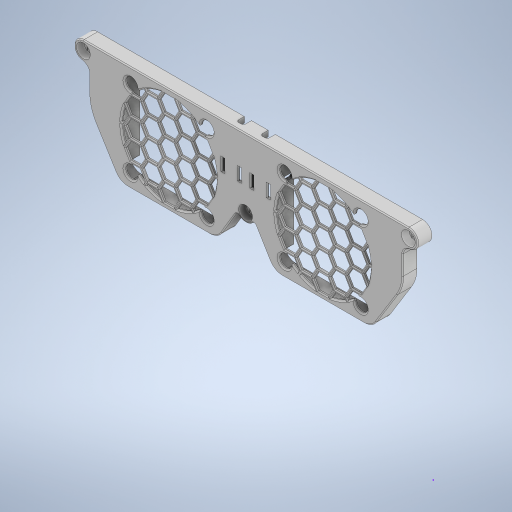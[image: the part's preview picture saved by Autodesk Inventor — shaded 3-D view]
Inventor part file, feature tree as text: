
AUTODESK INVENTOR PART (.ipt)
format: ipt  version: 2023.1 (Build 271208000, 208)  size: 2,170,368 bytes
history: native  units: mm
features: projected_geometry x12, sketch x10, extrude x9, other x7, reference x7, fillet x3, chamfer x3, delete_face x1, direct_edit x1, hole x1, move_body x1
ambient origin geometry x8: Origin, YZ Plane, XZ Plane, XY Plane, X Axis, Y Axis, Z Axis, Center Point
bodies: Volumenkörper2 (feature_tree), Volumenkörper1 (feature_tree)
feature tree (55):
  other  "Reparierte Geometrie1"
  sketch  "Skizze1"  dims[d0=10.0mm d1=0.0mm d2=0.0mm d3=0.0mm]
  extrude  "Extrusion1"  TaperAngle=0.0deg  [1 undecoded]
  extrude  "Extrusion2"  Depth=0.2mm TaperAngle=0.0deg
  delete_face  "Fläche löschen1"
  direct_edit  "Direktbearbeitung1"
  hole  "Bohrung1"  [1 undecoded]
  extrude  "Extrusion3"  Depth=40.4mm
  extrude  "Extrusion4"  Depth=4.1345mm
  extrude  "Extrusion5"  Depth=4.1345mm
  fillet  "Rundung1"  Radius=1.2mm
  chamfer  "Fase1"  Distance=0.6mm
  extrude  "Extrusion6"  TaperAngle=0.0deg  [1 undecoded]
  extrude  "Extrusion7"  Depth=1.0mm TaperAngle=0.0deg
  chamfer  "Fase2"  Distance=0.4mm
  extrude  "Extrusion8"  Depth=1.0mm TaperAngle=45.0deg
  chamfer  "Fase3"  Distance=2.0mm
  extrude  "Extrusion9"  Depth=1.0mm
  fillet  "Rundung2"  Radius=0.5555mm
  fillet  "Rundung3"  Radius=0.5555mm
  sketch  "Skizze53"  dims[d28=1.2mm d29=0.6mm d30=0.0mm d31=7.0mm d32=0.0mm d33=0.4mm d34=0.4mm d35=2.0mm d36=45.0deg d37=2.0mm d38=2.0mm d39=0.5555mm d40=0.5555mm d41=0.5555mm d42=0.5555mm d43=6.0mm d44=0.0mm d45=1.0mm d46=1.0mm d47=0.5mm d48=0.5mm d49=0.5mm d50=0.7mm d51=0.0mm d52=0.5mm d53=2.0mm d54=45.0deg d55=1.0mm d56=1.0mm d57=1.0mm d58=1.0mm d59=6.0mm d60=6.0mm d61=1.0mm d62=1.0mm d63=11.0mm d64=5.6mm d65=0.7mm d66=0.0mm d67=0.4mm d68=2.0mm d69=45.0deg d70=3.0mm d72=45.0deg d73=3.0mm d74=3.4mm d75=0.0mm d76=1.0mm d77=1.0mm]
  reference  "Referenz1"
  projected_geometry  "Projizierte Kontur1"
  sketch  "Skizze2"  dims[d4=0.0mm d5=0.0mm d6=1.0mm]
  projected_geometry  "Projizierte Kontur2"
  sketch  "Skizze3"  dims[d7=3.34mm d8=6.0mm d9=5.8mm d10=3.6mm d11=90.0deg d12=6.0mm d13=20.594885mm d14=0.2mm d15=0.0mm]
  projected_geometry  "Projizierte Kontur3"
  projected_geometry  "Projizierte Kontur4"
  projected_geometry  "Projizierte Kontur5"
  sketch  "Skizze4"  dims[d16=0.4mm d17=0.0mm d18=40.4mm]
  sketch  "Skizze5"  dims[d19=40.4mm d20=40.4mm]
  projected_geometry  "Projizierte Kontur6"
  projected_geometry  "Projizierte Kontur7"
  sketch  "Skizze6"  dims[d21=4.1345mm d22=4.1345mm]
  reference  "Referenz2"
  reference  "Referenz3"
  reference  "Referenz4"
  reference  "Referenz5"
  reference  "Referenz6"
  reference  "Referenz7"
  sketch  "Skizze7"  dims[d23=4.1345mm d24=4.1345mm d25=1.2mm]
  projected_geometry  "Projizierte Kontur8"
  projected_geometry  "Projizierte Kontur9"
  sketch  "Skizze8"  dims[d26=1.2mm]
  projected_geometry  "Projizierte Kontur10"
  projected_geometry  "Projizierte Kontur11"
  sketch  "Skizze9"  dims[d27=1.2mm]
  projected_geometry  "Projizierte Kontur12"
  other  "<userpath>\Desktop\GitHub\Voron-2-Mods\Mix\Octopus_Pro_FanCase\FanCase_Assembly.iam"
  other  "FanCase_Assembly.iam"
  other  "FanCase_Middle:1"
  move_body  "Verschieben1"
  other  "Noctua-Fan-NF-A4x10_40mm:2"
  other  "Noctua-NF-A4x10 v1:1"
  other  "Noctua-Fan-NF-A4x10_40mm:1"
note: 3 required parameter values undecoded (feature->parameter linkage not recoverable at this tier; creation-order binding heuristic only, values carry confidence <= 0.55)
